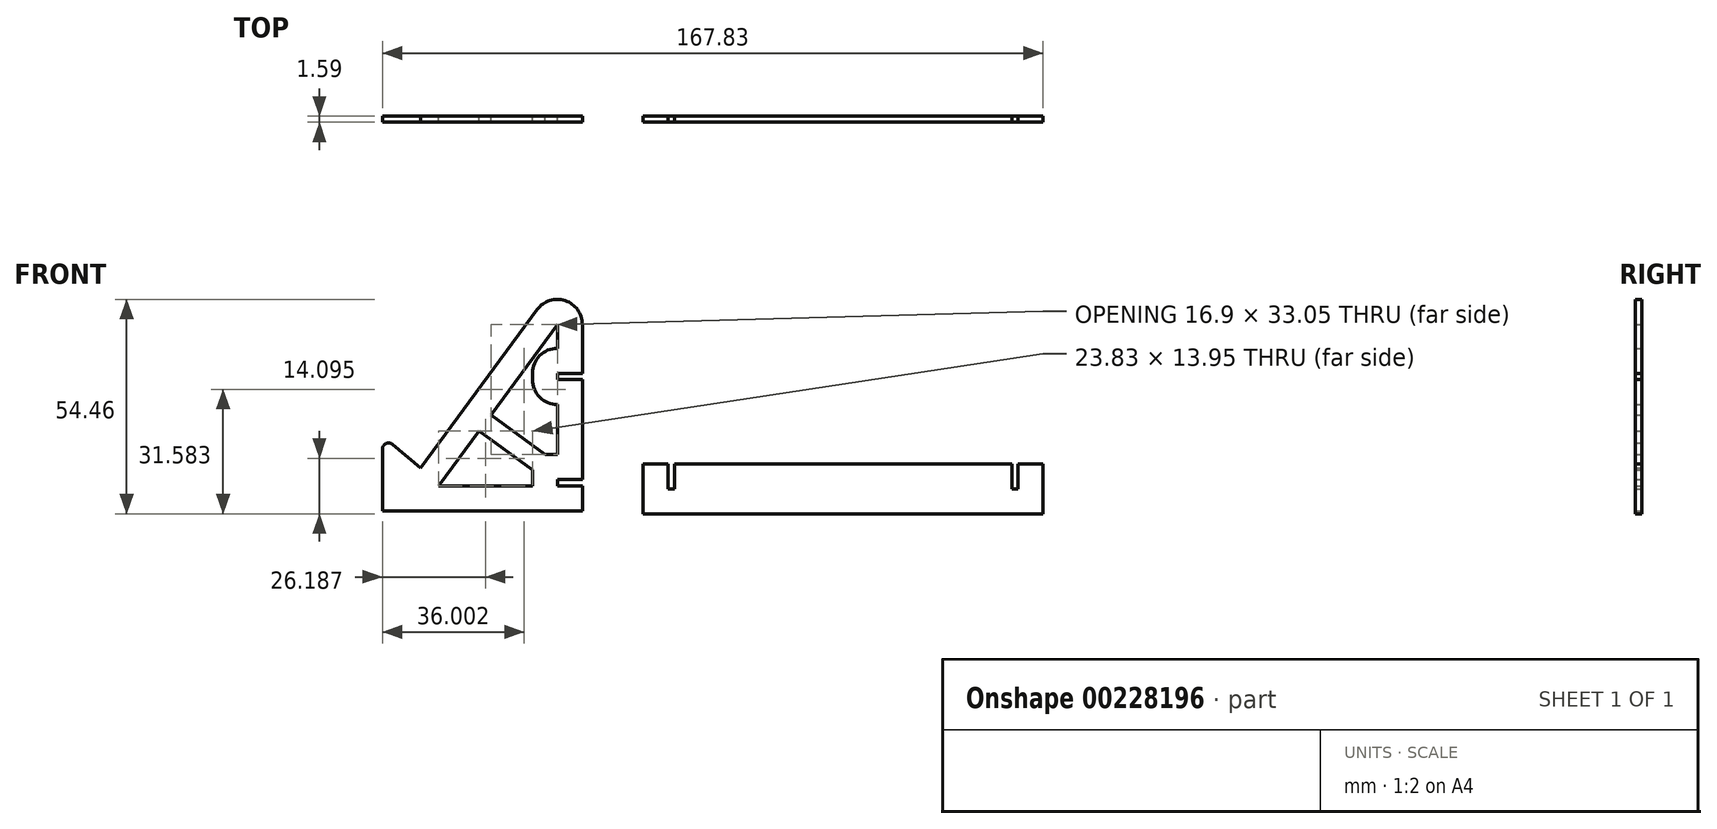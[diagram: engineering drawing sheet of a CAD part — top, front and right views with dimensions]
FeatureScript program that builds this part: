
annotation { "Feature Type Name" : "Feature", "Feature Type Description" : "" }
export const myFeature = defineFeature(function(context is Context, id is Id, definition is map)
    precondition{}
    {
        {
            var Q0;
            Q0=qCreatedBy(makeId("Front.planeOp"),FACE);
            var sketch = newSketch(context, id + "F0", { "sketchPlane" : qUnion([Q0])});
            skLineSegment(sketch, "E0", {"start": v(0, 0) * mm, "end": v(-50.8, 0) * mm});
            skLineSegment(sketch, "E1", {"start": v(-50.8, 0) * mm, "end": v(-50.8, 19.05) * mm});
            skLineSegment(sketch, "E2", {"start": v(-50.8, 19.05) * mm, "end": v(-41.07, 10.89) * mm});
            skLineSegment(sketch, "E3", {"start": v(-41.07, 10.89) * mm, "end": v(0, 66.68) * mm});
            skLineSegment(sketch, "E4", {"start": v(0, 66.68) * mm, "end": v(0, 34.93) * mm});
            skLineSegment(sketch, "E5.bottom", {"start": v(0, 6.35) * mm, "end": v(-6.35, 6.35) * mm});
            skLineSegment(sketch, "E5.top", {"start": v(0, 7.94) * mm, "end": v(-6.35, 7.94) * mm});
            skLineSegment(sketch, "E5.right", {"start": v(-6.35, 6.35) * mm, "end": v(-6.35, 7.94) * mm});
            skLineSegment(sketch, "E6.bottom", {"start": v(0, 33.34) * mm, "end": v(-6.35, 33.34) * mm});
            skLineSegment(sketch, "E6.top", {"start": v(0, 34.93) * mm, "end": v(-6.35, 34.93) * mm});
            skLineSegment(sketch, "E6.right", {"start": v(-6.35, 33.34) * mm, "end": v(-6.35, 34.93) * mm});
            skLineSegment(sketch, "E7.trimOffspring", {"start": v(0, 6.35) * mm, "end": v(0, 0) * mm});
            skLineSegment(sketch, "E8.trimOffspring", {"start": v(0, 33.34) * mm, "end": v(0, 7.94) * mm});
            skLineSegment(sketch, "E9.2", {"start": v(-6.35, 14.29) * mm, "end": v(-12.7, 14.29) * mm});
            skLineSegment(sketch, "E9.3", {"start": v(-6.35, 26.99) * mm, "end": v(-6.35, 26.99) * mm});
            skLineSegment(sketch, "E9.4", {"start": v(-12.7, 33.34) * mm, "end": v(-12.7, 34.93) * mm});
            skLineSegment(sketch, "E9.5", {"start": v(-12.7, 6.35) * mm, "end": v(-12.7, 14.29) * mm});
            skLineSegment(sketch, "E9.7", {"start": v(-12.7, 6.35) * mm, "end": v(-36.53, 6.35) * mm});
            skLineSegment(sketch, "E9.8", {"start": v(-6.35, 26.99) * mm, "end": v(-6.35, 14.29) * mm});
            skLineSegment(sketch, "E9.9", {"start": v(-6.35, 41.28) * mm, "end": v(-6.35, 41.28) * mm});
            skLineSegment(sketch, "E9.10", {"start": v(-36.53, 6.35) * mm, "end": v(-6.35, 47.34) * mm});
            skLineSegment(sketch, "E9.11", {"start": v(-6.35, 47.34) * mm, "end": v(-6.35, 41.28) * mm});
            skLineSegment(sketch, "E10", {"start": v(-12.7, 10.32) * mm, "end": v(-26.26, 20.3) * mm});
            skLineSegment(sketch, "E11", {"start": v(-9.52, 14.29) * mm, "end": v(-23.25, 24.39) * mm});
            skPoint(sketch, "E12.visualSharp", {"position": v(-12.7, 41.28) * mm});
            skArc(sketch, "E12.filletArc", {"start": v(-6.35, 41.28) * mm, "mid": v(-10.84, 39.42) * mm, "end": v(-12.7, 34.93) * mm});
            skPoint(sketch, "E13.visualSharp", {"position": v(-12.7, 26.99) * mm});
            skArc(sketch, "E13.filletArc", {"start": v(-12.7, 33.34) * mm, "mid": v(-10.84, 28.85) * mm, "end": v(-6.35, 26.99) * mm});
            skSolve(sketch);
        }
        {
            var Q0;
            {var subQ1=sQuery(id+"F0.wireOp",EDGE,"E0");Q0=makeQuery(id+"F0.imprint","IMPRINT",FACE,{"disambiguationData":[TD([[makeQuery(id+"F0.imprint","IMPRINT",EDGE,{"derivedFrom":subQ1}),-1.0]])]});}
            var Q1;
            {var subQ0=sQuery(id+"F0.wireOp",EDGE,"E10");Q1=makeQuery(id+"F0.imprint","IMPRINT",FACE,{"disambiguationData":[TD([[makeQuery(id+"F0.imprint","IMPRINT",EDGE,{"derivedFrom":subQ0}),-1.0]])]});}
            extrude(context, id + "F1", {"entities" : qUnion([Q0, Q1]), "depth" : 1.59 * mm});
        }
        {
            var Q0;
            Q0=qCreatedBy(makeId("Front.planeOp"),FACE);
            var sketch = newSketch(context, id + "F2", { "sketchPlane" : qUnion([Q0])});
            skLineSegment(sketch, "E14.bottom", {"start": v(15.43, 11.93) * mm, "end": v(66.23, 11.93) * mm});
            skLineSegment(sketch, "E14.top", {"start": v(15.43, -0.77) * mm, "end": v(66.23, -0.77) * mm});
            skLineSegment(sketch, "E14.left", {"start": v(15.43, 11.93) * mm, "end": v(15.43, -0.77) * mm});
            skLineSegment(sketch, "E14.right", {"start": v(66.23, 11.93) * mm, "end": v(66.23, -0.77) * mm});
            skLineSegment(sketch, "E15.bottom", {"start": v(21.78, 11.93) * mm, "end": v(23.37, 11.93) * mm});
            skLineSegment(sketch, "E15.top", {"start": v(21.78, 5.58) * mm, "end": v(23.37, 5.58) * mm});
            skLineSegment(sketch, "E15.left", {"start": v(21.78, 11.93) * mm, "end": v(21.78, 5.58) * mm});
            skLineSegment(sketch, "E15.right", {"start": v(23.37, 11.93) * mm, "end": v(23.37, 5.58) * mm});
            skLineSegment(sketch, "E16.MirrorCS", {"start": v(110.68, 5.58) * mm, "end": v(109.1, 5.58) * mm});
            skLineSegment(sketch, "E17.MirrorCS", {"start": v(110.68, 11.93) * mm, "end": v(109.1, 11.93) * mm});
            skLineSegment(sketch, "E18.MirrorCS", {"start": v(110.68, 11.93) * mm, "end": v(110.68, 5.58) * mm});
            skLineSegment(sketch, "E19.MirrorCS", {"start": v(117.03, 11.93) * mm, "end": v(117.03, -0.77) * mm});
            skLineSegment(sketch, "E20.MirrorCS", {"start": v(109.1, 11.93) * mm, "end": v(109.1, 5.58) * mm});
            skLineSegment(sketch, "E21.MirrorCS", {"start": v(117.03, -0.77) * mm, "end": v(66.23, -0.77) * mm});
            skLineSegment(sketch, "E22.MirrorCS", {"start": v(117.03, 11.93) * mm, "end": v(66.23, 11.93) * mm});
            skSolve(sketch);
        }
        {
            var Q0;
            Q0=makeQuery(id+"F2.imprint","IMPRINT",FACE,{"disambiguationData":[TD([[makeQuery(id+"F2.imprint","IMPRINT",EDGE,{"derivedFrom":sQuery(id+"F2.wireOp",EDGE,"E14.top")}),1.0]])]});
            var Q1;
            {var subQ2=sQuery(id+"F2.wireOp",EDGE,"E14.right");Q1=makeQuery(id+"F2.imprint","IMPRINT",FACE,{"disambiguationData":[TD([[makeQuery(id+"F2.imprint","IMPRINT",EDGE,{"derivedFrom":subQ2}),1.0]])]});}
            extrude(context, id + "F3", {"entities" : qUnion([Q0, Q1]), "depth" : 1.59 * mm});
        }
        {
            var Q0;
            Q0=makeQuery(id+"F1.opExtrude","SWEPT_EDGE",EDGE,{"disambiguationData":[OSD([sQuery(id+"F0.wireOp",EDGE,"E1"),sQuery(id+"F0.wireOp",EDGE,"E2")])]});
            fillet(context, id + "F4", {"entities" : qUnion([Q0]), "radius" : 1.59 * mm, "tangentPropagation" : true, "allowEdgeOverflow" : false});
        }
        {
            var Q0;
            Q0=makeQuery(id+"F1.opExtrude","SWEPT_EDGE",EDGE,{"disambiguationData":[OSD([sQuery(id+"F0.wireOp",EDGE,"E3"),sQuery(id+"F0.wireOp",EDGE,"E4")])]});
            fillet(context, id + "F5", {"entities" : qUnion([Q0]), "radius" : 6.35 * mm, "tangentPropagation" : true, "allowEdgeOverflow" : false});
        }
    });
